# Revit family: Faucet-Touchless-Lavatory-KOHLER-Strayt-K-103S37
name_source: partatom
category: Plumbing Fixtures
units: mm (PartAtom-declared; Revit-internal decimal feet)

## family parameters
Cut with Voids When Loaded = No
Host = Face
Maintain Annotation Orientation = No
OmniClass Number = 23.31.11.00
OmniClass Title = Faucets
Part Type = Normal
Room Calculation Point = No
Round Connector Dimension = Use Diameter
Shared = No

## types (4) — shared parameters
ADA Compliant = Yes
Apparent Load = 144 VA
Assembly Code = D2010
CW Connection = Yes
Cold Water Inlet = Cold Water Inlet
Date Modified = 06/30/2025
Default Elevation = 36"
Description = Touchless bathroom sink faucet with Kinesis sensor and mixer, AC-powered
Drain Included = Yes
Electrical Connector = Yes
Electrical Note = One circuit required, protected with Clasa A Ground-Fault Circuit-Interrupter (GFCI) or Residual Current Device (RCD)
Flow Rate = 1 GPM
HW Connection = Yes
Height = 5 7/16"
Hot Water Inlet = Hot Water Inlet
Length = 5 1/4"
Manufacturer = Kohler Co.
Master Format 2014 = 22 41 39
Master Format 2014 Name = Residential Faucet, Supplies, and Trim
Material = Premium Metal Construction
Pressure = 60.00 psi
Product Documentation Link = https://www.us.kohler.com
Product Name = Strayt
Product Page URL = http://www.us.kohler.com
Spout Reach = 5 1/4"
URL = https://www.us.kohler.com
Vent Connection = No
Voltage = 120 V
Waste Connection = No
Waste Water Outlet = Waste Water Outlet
WaterSense Certified = No
Width = 2 1/16"

## per-type parameters (varying)
| type | Finish | Model | Type |
| CP-Polished Chrome | Kohler-Metal-CP-Polished_Chrome | K-103S37-SANA-CP | 4 |
| 2MB-Vibrant Brushed Moderne Brass | Kohler-Metal-2MB-Vibrant_Brushed_Moderne_Brass | K-103S37-SANA-2MB | 1 |
| BN-Vibrant Brushed Nickel | Kohler-Metal-BN-Vibrant_Brushed_Nickel | K-103S37-SANA-BN | 2 |
| BL-Matte Black | Kohler-Metal-BL-Matte_Black | K-103S37-SANA-BL | 3 |

## geometry (parser evidence)
native form markers: Sweep x4
no freeform markers — native parametric forms only
